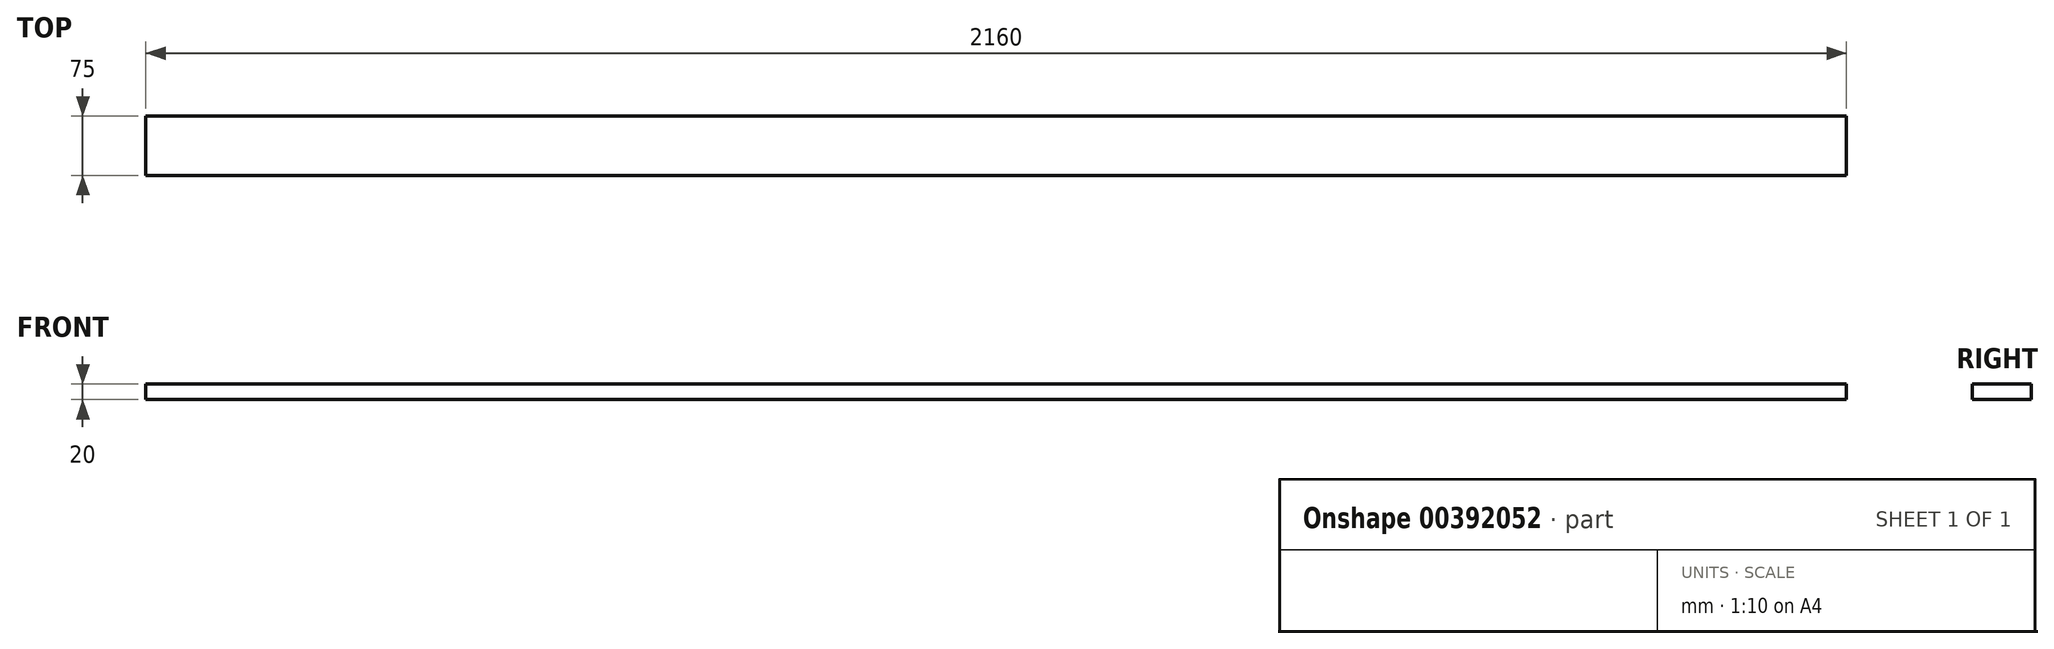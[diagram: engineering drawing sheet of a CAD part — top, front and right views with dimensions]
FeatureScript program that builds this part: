
annotation { "Feature Type Name" : "Feature", "Feature Type Description" : "" }
export const myFeature = defineFeature(function(context is Context, id is Id, definition is map)
    precondition{}
    {
        {
            var Q0;
            Q0=qCreatedBy(makeId("Right.planeOp"),FACE);
            var sketch = newSketch(context, id + "F0", { "sketchPlane" : qUnion([Q0])});
            skLineSegment(sketch, "E0.bottom", {"start": v(-37.5, 10) * mm, "end": v(37.5, 10) * mm});
            skLineSegment(sketch, "E0.top", {"start": v(-37.5, -10) * mm, "end": v(37.5, -10) * mm});
            skLineSegment(sketch, "E0.left", {"start": v(-37.5, 10) * mm, "end": v(-37.5, -10) * mm});
            skLineSegment(sketch, "E0.right", {"start": v(37.5, 10) * mm, "end": v(37.5, -10) * mm});
            skPoint(sketch, "E0.middle", {"position": v(0, 0) * mm});
            skSolve(sketch);
        }
        {
            var Q0;
            Q0=makeQuery(id+"F0.imprint","IMPRINT",FACE,{"disambiguationData":[TD([[makeQuery(id+"F0.imprint","IMPRINT",EDGE,{"derivedFrom":sQuery(id+"F0.wireOp",EDGE,"E0.bottom")}),-1.0]])]});
            extrude(context, id + "F1", {"entities" : qUnion([Q0]), "endBound" : BoundingType.SYMMETRIC, "depth" : 2160 * mm});
        }
    });
